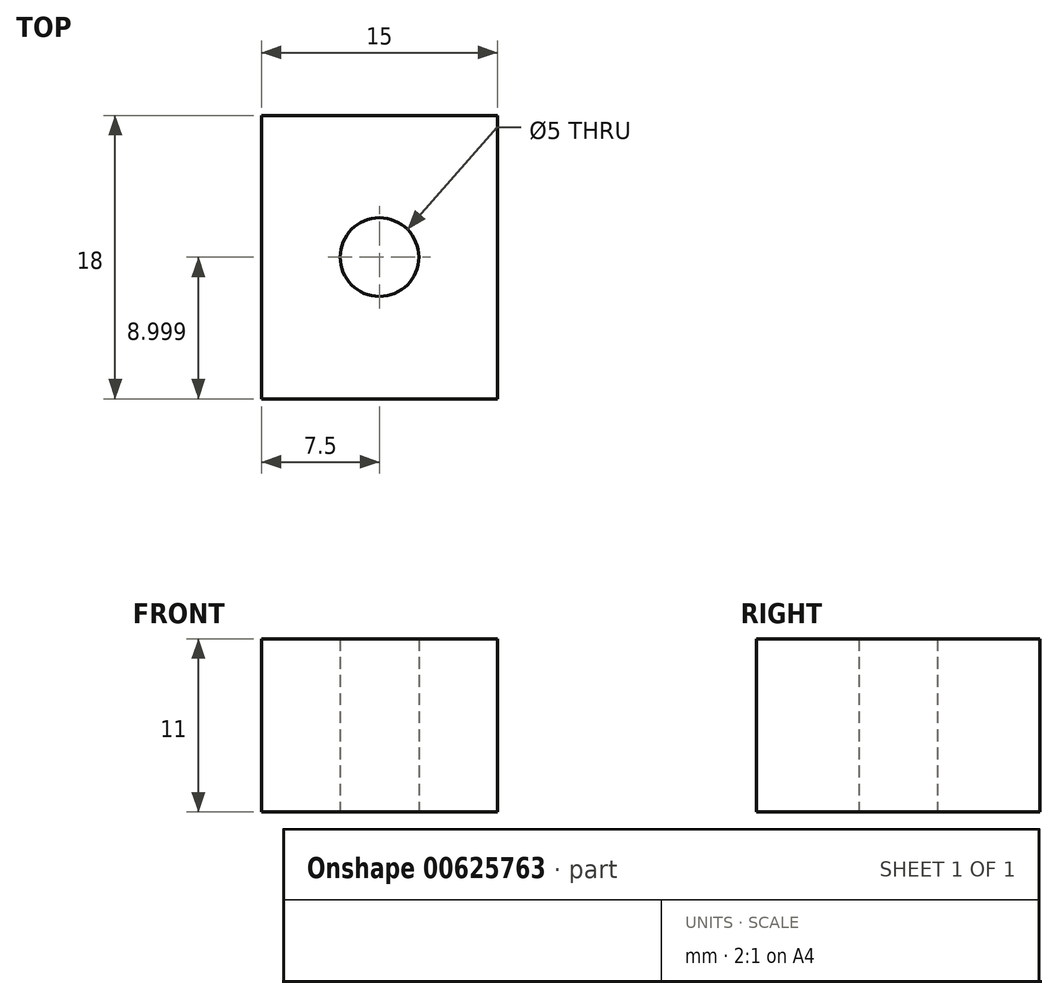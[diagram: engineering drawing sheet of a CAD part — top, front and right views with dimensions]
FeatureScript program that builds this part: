
annotation { "Feature Type Name" : "Feature", "Feature Type Description" : "" }
export const myFeature = defineFeature(function(context is Context, id is Id, definition is map)
    precondition{}
    {
        {
            var Q0;
            Q0=qCreatedBy(makeId("Top.planeOp"),FACE);
            var sketch = newSketch(context, id + "F0", { "sketchPlane" : qUnion([Q0])});
            skLineSegment(sketch, "E0.bottom", {"start": v(15, -38.38) * mm, "end": v(0, -38.38) * mm});
            skLineSegment(sketch, "E0.top", {"start": v(15, -20.38) * mm, "end": v(0, -20.38) * mm});
            skLineSegment(sketch, "E0.left", {"start": v(15, -38.38) * mm, "end": v(15, -20.38) * mm});
            skLineSegment(sketch, "E0.right", {"start": v(0, -38.38) * mm, "end": v(0, -20.38) * mm});
            skLineSegment(sketch, "E1", {"start": v(7.5, -29.38) * mm, "end": v(15, -38.38) * mm, "construction": true});
            skLineSegment(sketch, "E2", {"start": v(0, -38.38) * mm, "end": v(7.5, -29.38) * mm, "construction": true});
            skCircle(sketch, "E3", {"center": v(7.5, -29.38) * mm, "radius": 2.5 * mm});
            skSolve(sketch);
        }
        {
            var Q0;
            Q0 = qSketchRegion(id + "F0", true);
            extrude(context, id + "F1", {"entities" : qUnion([Q0]), "depth" : 11 * mm, "offsetDistance" : 25 * mm});
        }
    });
